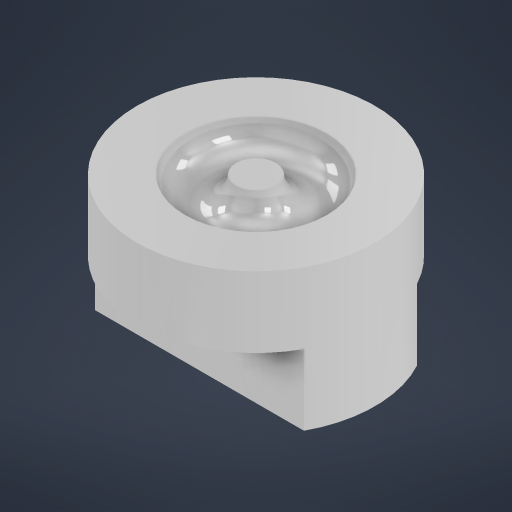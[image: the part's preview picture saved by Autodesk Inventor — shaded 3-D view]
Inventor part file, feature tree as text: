
AUTODESK INVENTOR PART (.ipt)
format: ipt  version: 2024 (Build 280153000, 153)  size: 237,568 bytes
history: native  units: in
note: dims shown in document units (in); Inventor stores cm internally (conversion verified against a paired STEP export)
features: sketch x3, extrude x2, revolve x1, shell x1
ambient origin geometry x8: Origin, YZ Plane, XZ Plane, XY Plane, X Axis, Y Axis, Z Axis, Center Point
bodies: Solid1 (feature_tree)
feature tree (7):
  extrude  "Extrusion1"  Depth=1.9685in TaperAngle=0.0deg
  revolve  "Revolution1"  [1 undecoded]
  extrude  "Extrusion2"  Depth=0.9843in
  shell  "Shell1"  Thickness=0.7874in
  sketch  "Sketch1"  dims[d0=3.3071in d1=1.9685in d2=0.0in]
  sketch  "Sketch3"  dims[d4=0.7087in d5=1.2598in]
  sketch  "Sketch4"  dims[d6=90.0deg d7=0.9843in d8=0.7874in d9=3.937in d10=0.0in d11=0.1969in]
note: 1 required parameter value undecoded (feature->parameter linkage not recoverable at this tier; creation-order binding heuristic only, values carry confidence <= 0.55)
